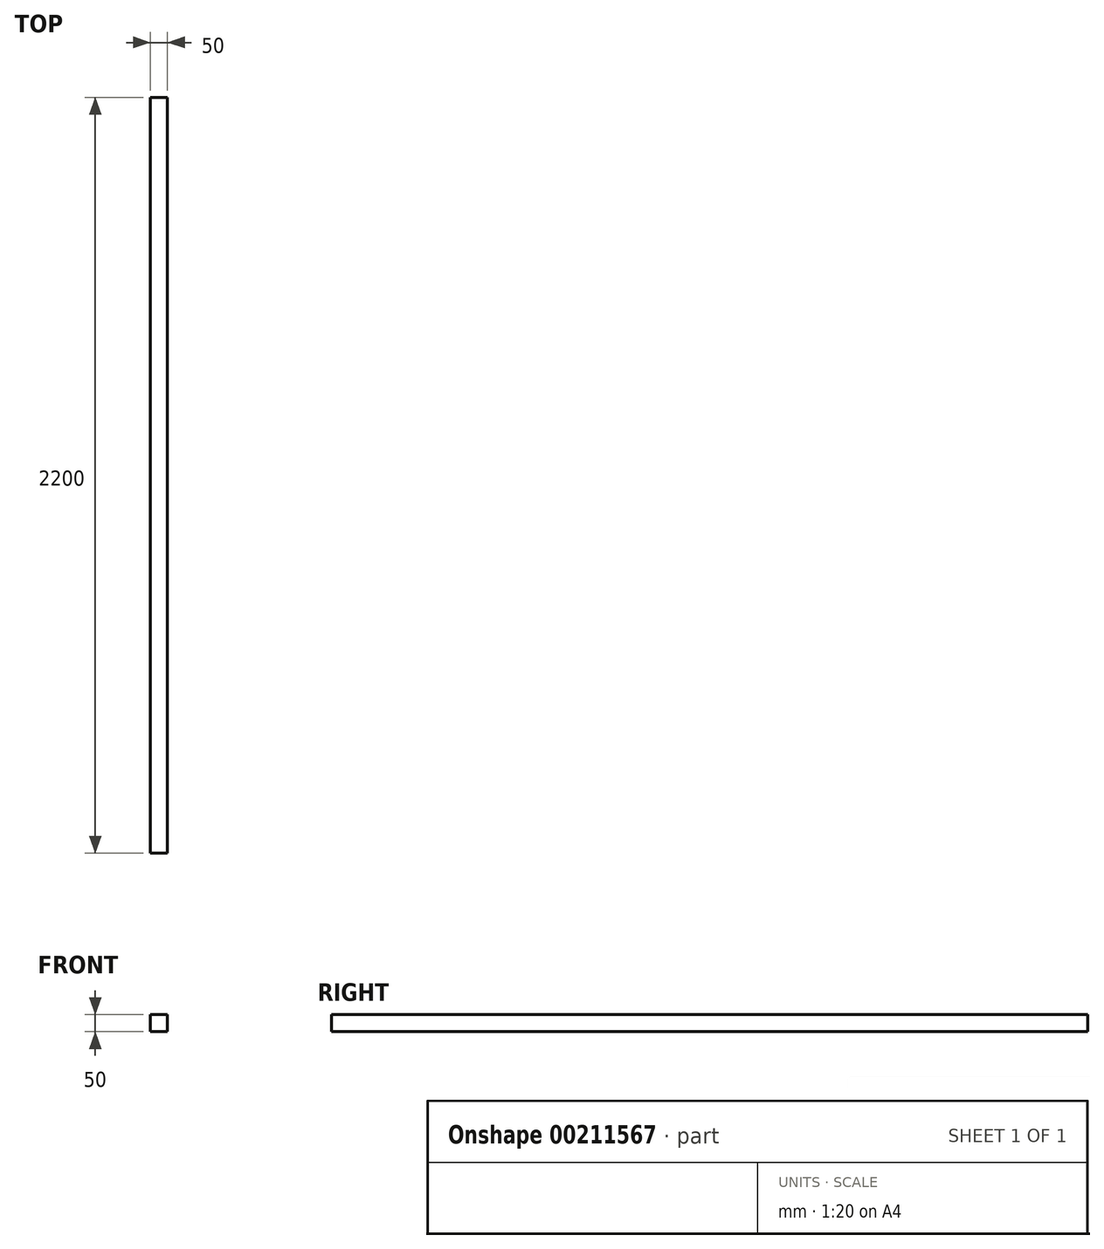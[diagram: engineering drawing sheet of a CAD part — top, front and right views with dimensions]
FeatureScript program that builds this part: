
annotation { "Feature Type Name" : "Feature", "Feature Type Description" : "" }
export const myFeature = defineFeature(function(context is Context, id is Id, definition is map)
    precondition{}
    {
        {
            var Q0;
            Q0=qCreatedBy(makeId("Front.planeOp"),FACE);
            var sketch = newSketch(context, id + "F0", { "sketchPlane" : qUnion([Q0])});
            skLineSegment(sketch, "E0.bottom", {"start": v(0, 0) * mm, "end": v(50, 0) * mm});
            skLineSegment(sketch, "E0.top", {"start": v(0, 50) * mm, "end": v(50, 50) * mm});
            skLineSegment(sketch, "E0.left", {"start": v(0, 0) * mm, "end": v(0, 50) * mm});
            skLineSegment(sketch, "E0.right", {"start": v(50, 0) * mm, "end": v(50, 50) * mm});
            skSolve(sketch);
        }
        {
            var Q0;
            Q0 = qSketchRegion(id + "F0", true);
            extrude(context, id + "F1", {"entities" : qUnion([Q0]), "oppositeDirection" : true, "depth" : 2200 * mm});
        }
    });
